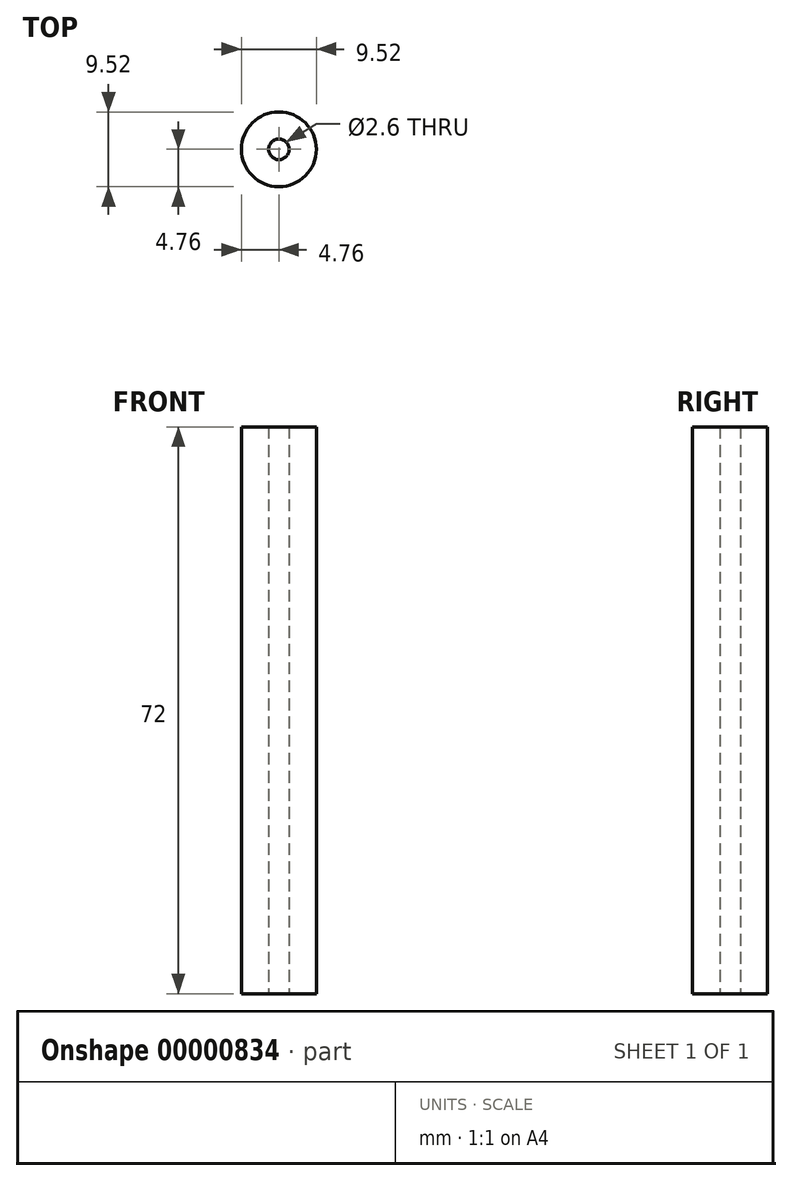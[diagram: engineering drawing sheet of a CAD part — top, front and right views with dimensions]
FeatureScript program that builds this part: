
annotation { "Feature Type Name" : "Feature", "Feature Type Description" : "" }
export const myFeature = defineFeature(function(context is Context, id is Id, definition is map)
    precondition{}
    {
        {
            var Q0;
            Q0=qCreatedBy(makeId("Top.planeOp"),FACE);
            var sketch = newSketch(context, id + "F0", { "sketchPlane" : qUnion([Q0])});
            skCircle(sketch, "E0", {"center": v(0, 0) * mm, "radius": 4.76 * mm});
            skSolve(sketch);
        }
        {
            var Q0;
            Q0=makeQuery(id+"F0.imprint","IMPRINT",FACE,{"disambiguationData":[TD([[makeQuery(id+"F0.imprint","IMPRINT",EDGE,{"derivedFrom":sQuery(id+"F0.wireOp",EDGE,"E0")}),1.0]])]});
            extrude(context, id + "F1", {"entities" : qUnion([Q0]), "depth" : 72 * mm});
        }
        {
            var Q0;
            Q0=makeQuery(id+"F1.opExtrude","CAP_FACE",FACE,{"disambiguationData":[OSD([sQuery(id+"F0.wireOp",EDGE,"E0")])],"isStart":true});
            var sketch = newSketch(context, id + "F2", { "sketchPlane" : qUnion([Q0])});
            skCircle(sketch, "E1", {"center": v(0, 0) * mm, "radius": 1.3 * mm});
            skSolve(sketch);
        }
        {
            var Q0;
            Q0=makeQuery(id+"F2.imprint","IMPRINT",FACE,{"disambiguationData":[TD([[makeQuery(id+"F2.imprint","IMPRINT",EDGE,{"derivedFrom":sQuery(id+"F2.wireOp",EDGE,"E1")}),1.0]])]});
            extrude(context, id + "F3", {"entities" : qUnion([Q0]), "operationType" : NewBodyOperationType.REMOVE, "endBound" : BoundingType.THROUGH_ALL, "oppositeDirection" : true, "depth" : 25 * mm});
        }
    });
